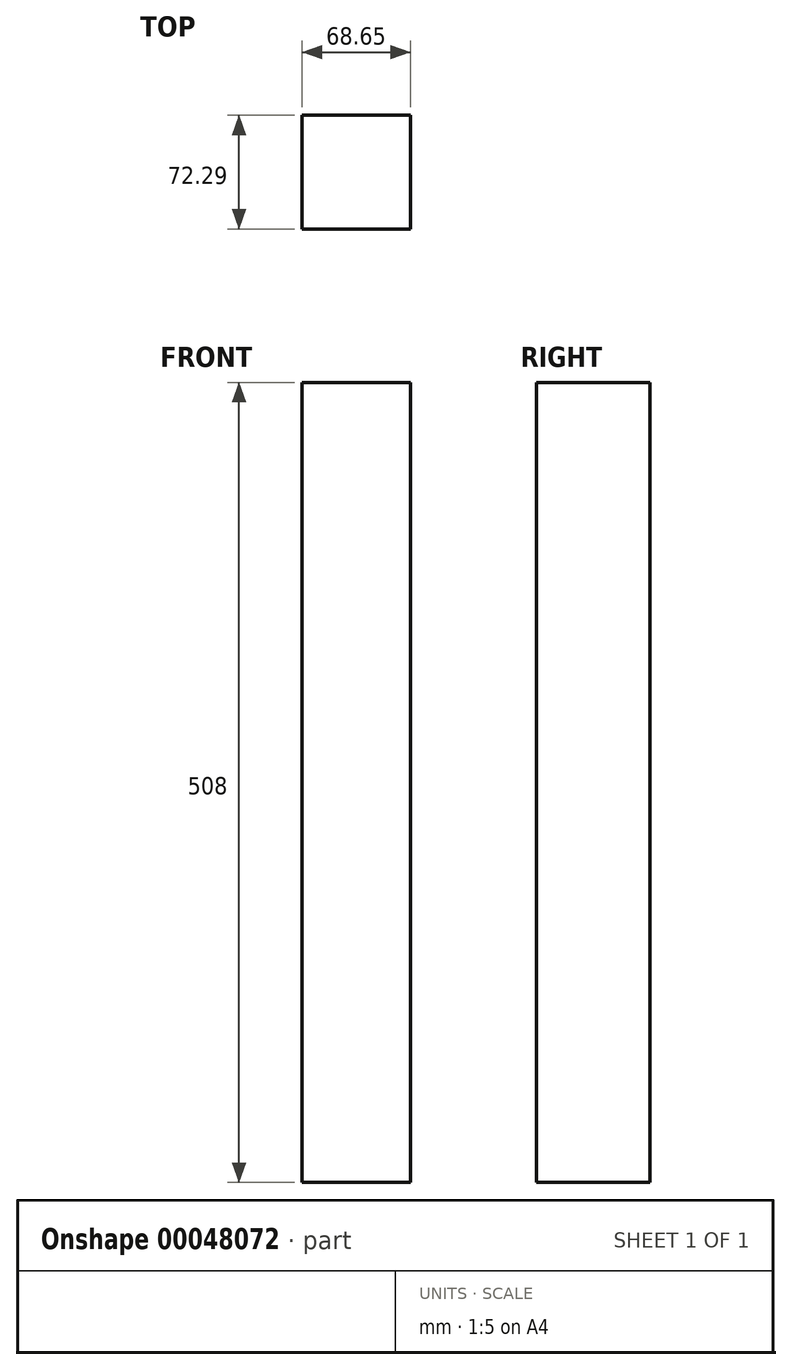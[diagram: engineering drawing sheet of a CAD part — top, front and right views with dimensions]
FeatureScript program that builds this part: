
annotation { "Feature Type Name" : "Feature", "Feature Type Description" : "" }
export const myFeature = defineFeature(function(context is Context, id is Id, definition is map)
    precondition{}
    {
        {
            var Q0;
            Q0=qCreatedBy(makeId("Top.planeOp"),FACE);
            var sketch = newSketch(context, id + "F0", { "sketchPlane" : qUnion([Q0])});
            skLineSegment(sketch, "E0.bottom", {"start": v(-29.96, 29.7) * mm, "end": v(38.7, 29.7) * mm});
            skLineSegment(sketch, "E0.top", {"start": v(-29.96, -42.6) * mm, "end": v(38.7, -42.6) * mm});
            skLineSegment(sketch, "E0.left", {"start": v(-29.96, 29.7) * mm, "end": v(-29.96, -42.6) * mm});
            skLineSegment(sketch, "E0.right", {"start": v(38.7, 29.7) * mm, "end": v(38.7, -42.6) * mm});
            skSolve(sketch);
        }
        {
            var Q0;
            Q0=makeQuery(id+"F0.imprint","IMPRINT",FACE,{"disambiguationData":[TD([[makeQuery(id+"F0.imprint","IMPRINT",EDGE,{"derivedFrom":sQuery(id+"F0.wireOp",EDGE,"E0.bottom")}),-1.0]])]});
            extrude(context, id + "F1", {"entities" : qUnion([Q0]), "depth" : 508 * mm});
        }
    });
